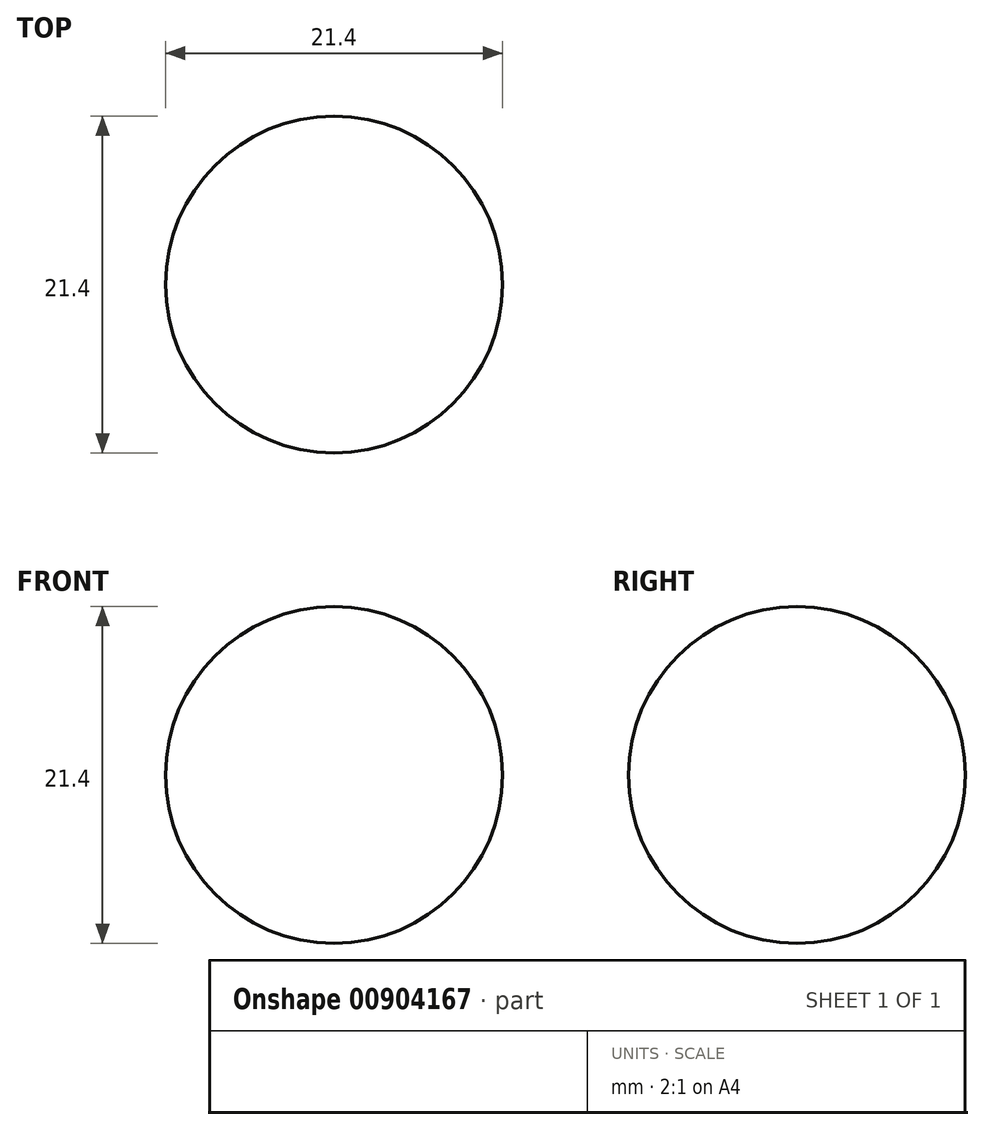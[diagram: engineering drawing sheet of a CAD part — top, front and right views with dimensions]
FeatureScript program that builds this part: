
annotation { "Feature Type Name" : "Feature", "Feature Type Description" : "" }
export const myFeature = defineFeature(function(context is Context, id is Id, definition is map)
    precondition{}
    {
        {
            var Q0;
            Q0=qCreatedBy(makeId("Top.planeOp"),FACE);
            var sketch = newSketch(context, id + "F0", { "sketchPlane" : qUnion([Q0])});
            skCircle(sketch, "E0", {"center": v(0, 0) * mm, "radius": 10.7 * mm});
            skSolve(sketch);
        }
        {
            var Q0;
            Q0=makeQuery(id+"F0.imprint","IMPRINT",FACE,{"disambiguationData":[TD([[makeQuery(id+"F0.imprint","IMPRINT",EDGE,{"derivedFrom":sQuery(id+"F0.wireOp",EDGE,"E0")}),1.0]])]});
            extrude(context, id + "F1", {"entities" : qUnion([Q0]), "depth" : 10.7 * mm, "offsetDistance" : 25 * mm, "hasSecondDirection" : true, "secondDirectionOppositeDirection" : true, "secondDirectionDepth" : 10.7 * mm});
        }
        {
            var Q0;
            Q0=makeQuery(id+"F1.opExtrude","SWEPT_FACE",FACE,{"disambiguationData":[OSD([sQuery(id+"F0.wireOp",EDGE,"E0")])]});
            fillet(context, id + "F2", {"entities" : qUnion([Q0]), "radius" : 10.7 * mm, "tangentPropagation" : true, "allowEdgeOverflow" : false});
        }
    });
